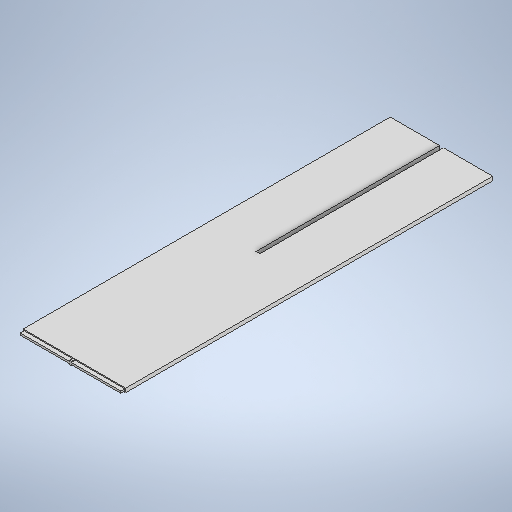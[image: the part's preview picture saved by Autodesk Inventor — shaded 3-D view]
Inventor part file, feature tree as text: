
AUTODESK INVENTOR PART (.ipt)
format: ipt  version: 2025.2 (Build 292293000, 293)  size: 345,088 bytes
history: native  units: mm
features: extrude x9, sketch x9, projected_geometry x1
ambient origin geometry x8: Origin, YZ Plane, XZ Plane, XY Plane, X Axis, Y Axis, Z Axis, Center Point
bodies: Solid1 (feature_tree)
feature tree (19):
  extrude  "Extrusion1"  Depth=447.675mm
  extrude  "Extrusion2"  Depth=4.7625mm TaperAngle=0.0deg
  extrude  "Extrusion3"  Depth=6.0mm
  extrude  "Extrusion4"  Depth=10.0mm TaperAngle=0.0deg
  extrude  "Extrusion5"  Depth=4.763mm
  extrude  "Extrusion6"  Depth=2.374mm
  extrude  "Extrusion7"  Depth=4.763mm
  extrude  "Extrusion8"  Depth=12.5mm
  extrude  "Extrusion9"  Depth=10.0mm TaperAngle=0.0deg
  sketch  "Sketch1"  dims[d0=50.0mm d1=447.675mm]
  sketch  "Sketch2"  dims[d2=4.7625mm d3=0.0mm d9=4.7625mm d10=0.0mm]
  sketch  "Sketch3"  dims[d11=25.0mm d13=6.0mm]
  sketch  "Sketch4"  dims[d14=6.0mm d15=10.0mm d16=0.0mm]
  projected_geometry  "Projected Loop1"
  sketch  "Sketch7"  dims[d17=158.838mm d18=0.0mm d20=4.763mm]
  sketch  "Sketch8"  dims[d21=223.837mm d22=0.0mm d25=2.374mm]
  sketch  "Sketch9"  dims[d26=4.763mm d27=0.0mm d28=25.0mm]
  sketch  "Sketch10"  dims[d29=10.0mm d30=0.0mm d31=12.5mm]
  sketch  "Sketch11"  dims[d32=10.0mm d33=0.0mm d37=10.0mm d38=0.0mm]
